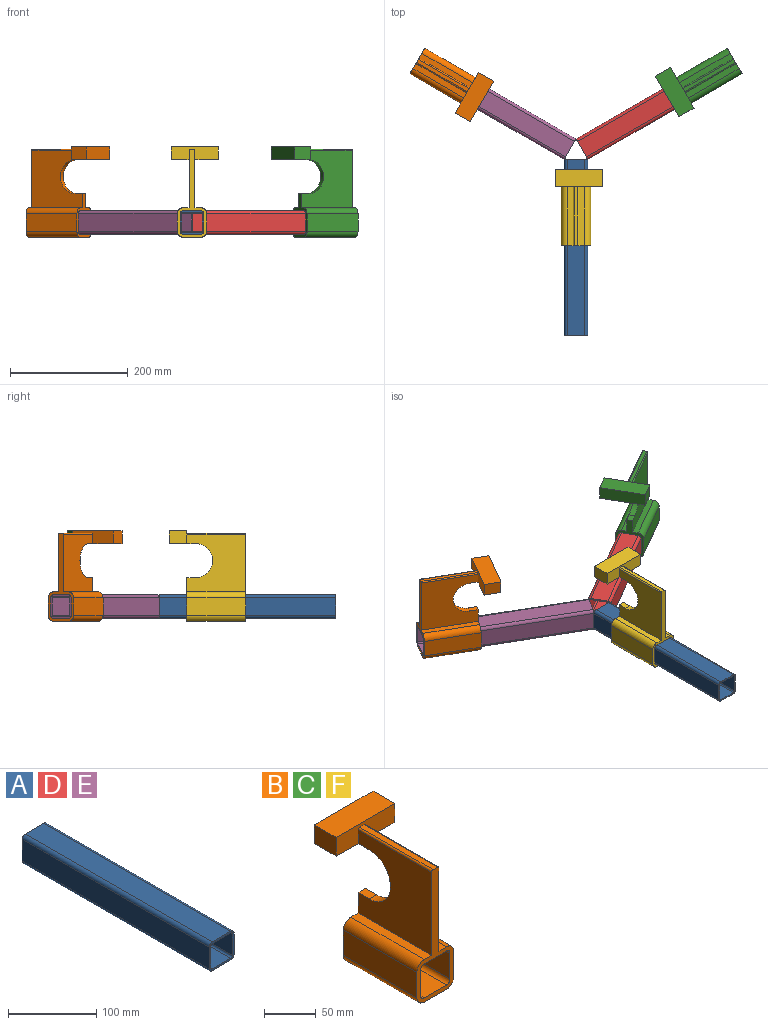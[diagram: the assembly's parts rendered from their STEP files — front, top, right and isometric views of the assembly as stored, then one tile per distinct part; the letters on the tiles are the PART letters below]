
ASSEMBLY  parts=6 mates=3
PART A: 18 faces, bbox 40x300x40 mm
  f0: plane 300x30mm, normal (1,0,0), area 9000mm2, adj f1,f15,f16,f17
  f1: cylinder r=5mm len=300mm, axis (0,1,0), area 2356.2mm2, adj f0,f2,f16,f17
  f2: plane 300x30mm, normal (0,0,1), area 9000mm2, adj f1,f3,f16,f17
  f3: cylinder r=5mm len=300mm, axis (0,1,0), area 2356.2mm2, adj f2,f4,f16,f17
  f4: plane 300x30mm, normal (-1,0,0), area 9000mm2, adj f3,f5,f16,f17
  f5: cylinder r=5mm len=300mm, axis (0,1,0), area 2356.2mm2, adj f4,f6,f16,f17
  f6: plane 300x30mm, normal (0,0,-1), area 9000mm2, adj f5,f15,f16,f17
  f7: cylinder r=2.5mm len=300mm, axis (0,1,0), area 1178.1mm2, adj f8,f14,f16,f17
  f8: plane 300x30mm, normal (0,0,-1), area 9000mm2, adj f7,f9,f16,f17
  f9: cylinder r=2.5mm len=300mm, axis (0,1,0), area 1178.1mm2, adj f8,f10,f16,f17
  f10: plane 300x30mm, normal (-1,0,0), area 9000mm2, adj f9,f11,f16,f17
  f11: cylinder r=2.5mm len=300mm, axis (0,1,0), area 1178.1mm2, adj f10,f12,f16,f17
  f12: plane 300x30mm, normal (0,0,1), area 9000mm2, adj f11,f13,f16,f17
  f13: cylinder r=2.5mm len=300mm, axis (0,1,0), area 1178.1mm2, adj f12,f14,f16,f17
  f14: plane 300x30mm, normal (1,0,0), area 9000mm2, adj f7,f13,f16,f17
  f15: cylinder r=5mm len=300mm, axis (0,1,0), area 2356.2mm2, adj f0,f6,f16,f17
  f16: plane 40x40mm, normal (0,1,0), area 358.9mm2, adj f0,f1,f2,f3,f4,f5,f6,f7
  f17: plane 40x40mm, normal (0,-1,0), area 358.9mm2, adj f0,f1,f2,f3,f4,f5,f6,f7
PART B: 32 faces, bbox 80x129.6x154 mm
  f0: plane 100x30mm, normal (-1,0,0), area 3000mm2, adj f1,f21,f22,f23
  f1: cylinder r=10mm len=100mm, axis (0,1,0), area 1570.8mm2, adj f0,f2,f22,f23
  f2: plane 100x30mm, normal (0,0,-1), area 3000mm2, adj f1,f3,f22,f23
  f3: cylinder r=10mm len=100mm, axis (0,1,0), area 1570.8mm2, adj f2,f4,f22,f23
  f4: plane 100x30mm, normal (1,0,0), area 3000mm2, adj f3,f5,f22,f23
  f5: cylinder r=10mm len=100mm, axis (0,1,0), area 1570.8mm2, adj f4,f6,f22,f23
  f6: plane 100x10mm, normal (0,0,1), area 1000mm2, adj f5,f7,f22,f23
  f7: plane 100x98mm, normal (1,0,0), area 7609mm2, adj f6,f8,f22,f23,f24,f25,f26,f27
  f8: cylinder r=2mm len=100mm, axis (0,1,0), area 314.2mm2, adj f7,f9,f22,f27
  f9: plane 100x6mm, normal (0,0,1), area 600mm2, adj f8,f10,f22,f27
  f10: cylinder r=2mm len=100mm, axis (0,1,0), area 314.2mm2, adj f9,f11,f22,f27
  f11: plane 100x98mm, normal (-1,0,0), area 7609mm2, adj f10,f12,f22,f23,f24,f25,f26,f27
  f12: plane 100x10mm, normal (0,0,1), area 1000mm2, adj f11,f21,f22,f23
  f13: cylinder r=5mm len=100mm, axis (0,1,0), area 785.4mm2, adj f14,f20,f22,f23
  f14: plane 100x30mm, normal (0,0,-1), area 3000mm2, adj f13,f15,f22,f23
  f15: cylinder r=5mm len=100mm, axis (0,1,0), area 785.4mm2, adj f14,f16,f22,f23
  f16: plane 100x30mm, normal (-1,0,0), area 3000mm2, adj f15,f17,f22,f23
  f17: cylinder r=5mm len=100mm, axis (0,1,0), area 785.4mm2, adj f16,f18,f22,f23
  f18: plane 100x30mm, normal (0,0,1), area 3000mm2, adj f17,f19,f22,f23
  f19: cylinder r=5mm len=100mm, axis (0,1,0), area 785.4mm2, adj f18,f20,f22,f23
  f20: plane 100x30mm, normal (1,0,0), area 3000mm2, adj f13,f19,f22,f23
  f21: cylinder r=10mm len=100mm, axis (0,1,0), area 1570.8mm2, adj f0,f12,f22,f23
  f22: plane 150x50mm, normal (0,-1,0), area 1833.9mm2, adj f0,f1,f2,f3,f4,f5,f6,f7
  f23: plane 73.98x50mm, normal (0,1,0), area 1075.4mm2, adj f0,f1,f2,f3,f4,f5,f6,f7
  f24: cylinder r=29mm len=58mm, axis (1,0,0), area 913.9mm2, adj f7,f11,f25,f26
  f25: plane 15x10mm, normal (0,0,1), area 150mm2, adj f7,f11,f23,f24
  f26: plane 80x44.36mm, normal (0,0,-1), area 2518.4mm2, adj f7,f11,f24,f27,f28,f30,f31
  f27: plane 80x21.99mm, normal (0,-1,0), area 1580.6mm2, adj f7,f8,f9,f10,f11,f26,f29,f30
  f28: plane 80x21.99mm, normal (0,1,0), area 1759.2mm2, adj f26,f29,f30,f31
  f29: plane 80x29.64mm, normal (0,0,1), area 2371.2mm2, adj f27,f28,f30,f31
  f30: plane 29.64x21.99mm, normal (1,0,0), area 651.8mm2, adj f26,f27,f28,f29
  f31: plane 29.64x21.99mm, normal (-1,0,0), area 651.8mm2, adj f26,f27,f28,f29
PART C: same geometry as B
PART D: same geometry as A
PART E: same geometry as A
PART F: same geometry as B
PLACE A t=(15.09,175.46,-11.66)mm fixed
PLACE B rot(axis=(0,0,-1),120deg) t=(-195.62,275.46,-13.79)mm
PLACE C rot(axis=(0,0,1),120deg) t=(170.82,310.05,-13.79)mm
PLACE D rot(axis=(0,0,1),120deg) t=(-1.13,207.89,-11.79)mm fixed
PLACE E rot(axis=(0,0,-1),120deg) t=(-21.16,177.62,-11.79)mm fixed
PLACE F t=(17.59,128.9,-13.66)mm
MATE planar E.f4 <-> B.f20  axis (0.5,0.87,0) through (-132.32,285.1,0)mm
MATE planar D.f4 <-> C.f20  axis (0.5,-0.87,0) through (147.52,250.41,0)mm
MATE planar A.f4 <-> F.f20  axis (-1,0,0) through (-22.41,25.46,0.13)mm
